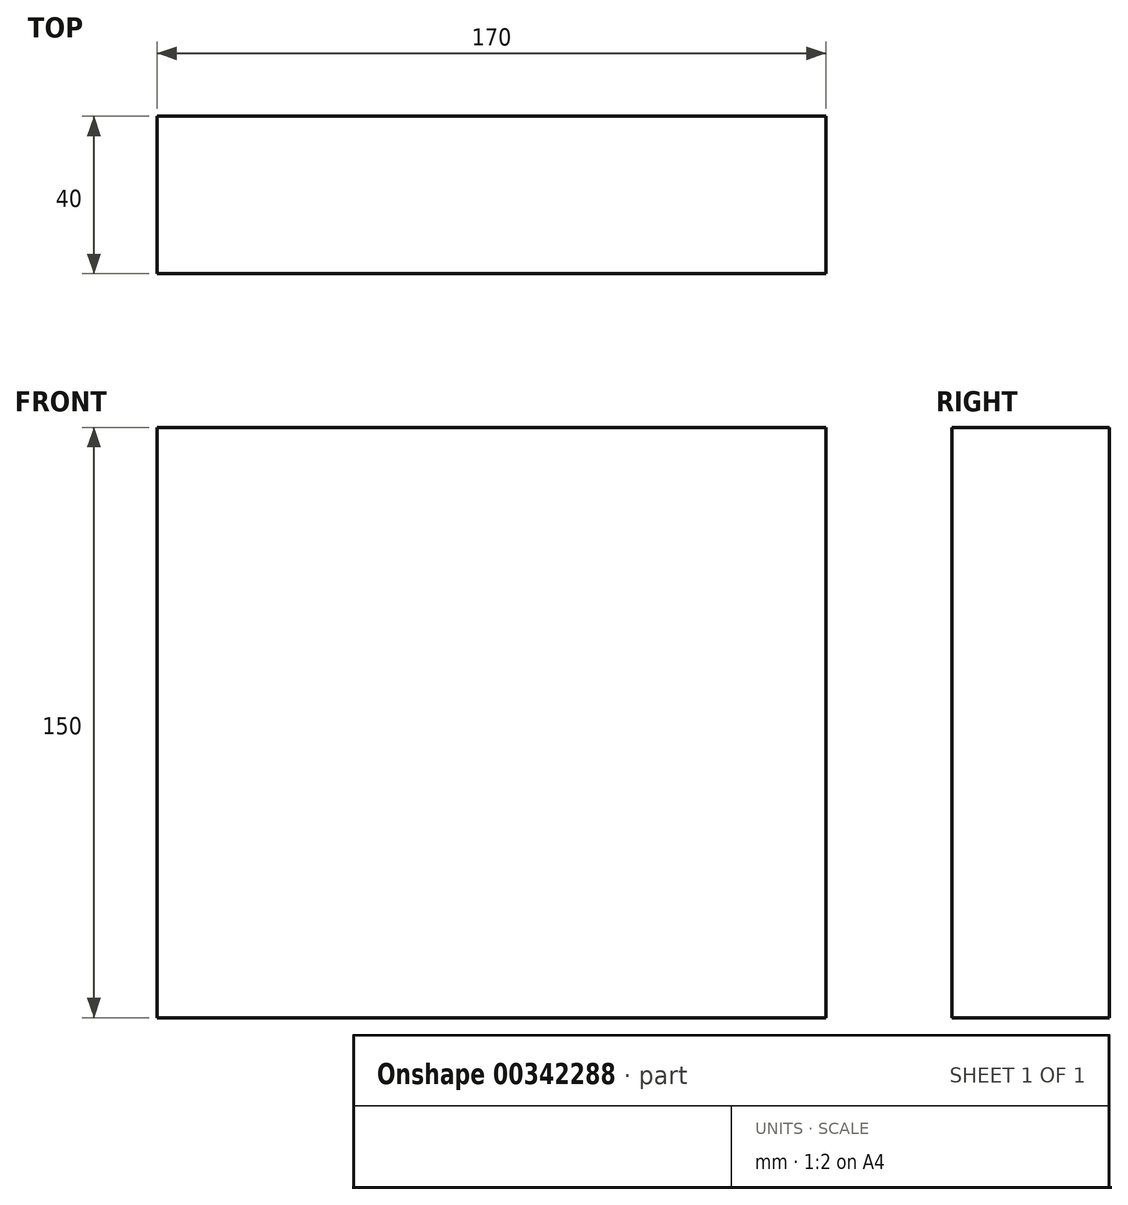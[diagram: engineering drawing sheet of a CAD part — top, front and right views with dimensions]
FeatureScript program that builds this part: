
annotation { "Feature Type Name" : "Feature", "Feature Type Description" : "" }
export const myFeature = defineFeature(function(context is Context, id is Id, definition is map)
    precondition{}
    {
        {
            var Q0;
            Q0=qCreatedBy(makeId("Front.planeOp"),FACE);
            var sketch = newSketch(context, id + "F0", { "sketchPlane" : qUnion([Q0])});
            skLineSegment(sketch, "E0.bottom", {"start": v(0, 0) * mm, "end": v(170, 0) * mm});
            skLineSegment(sketch, "E0.top", {"start": v(0, 150) * mm, "end": v(170, 150) * mm});
            skLineSegment(sketch, "E0.left", {"start": v(0, 0) * mm, "end": v(0, 150) * mm});
            skLineSegment(sketch, "E0.right", {"start": v(170, 0) * mm, "end": v(170, 150) * mm});
            skSolve(sketch);
        }
        {
            var Q0;
            Q0=makeQuery(id+"F0.imprint","IMPRINT",FACE,{"disambiguationData":[TD([[makeQuery(id+"F0.imprint","IMPRINT",EDGE,{"derivedFrom":sQuery(id+"F0.wireOp",EDGE,"E0.bottom")}),1.0]])]});
            extrude(context, id + "F1", {"entities" : qUnion([Q0]), "depth" : 40 * mm});
        }
    });
